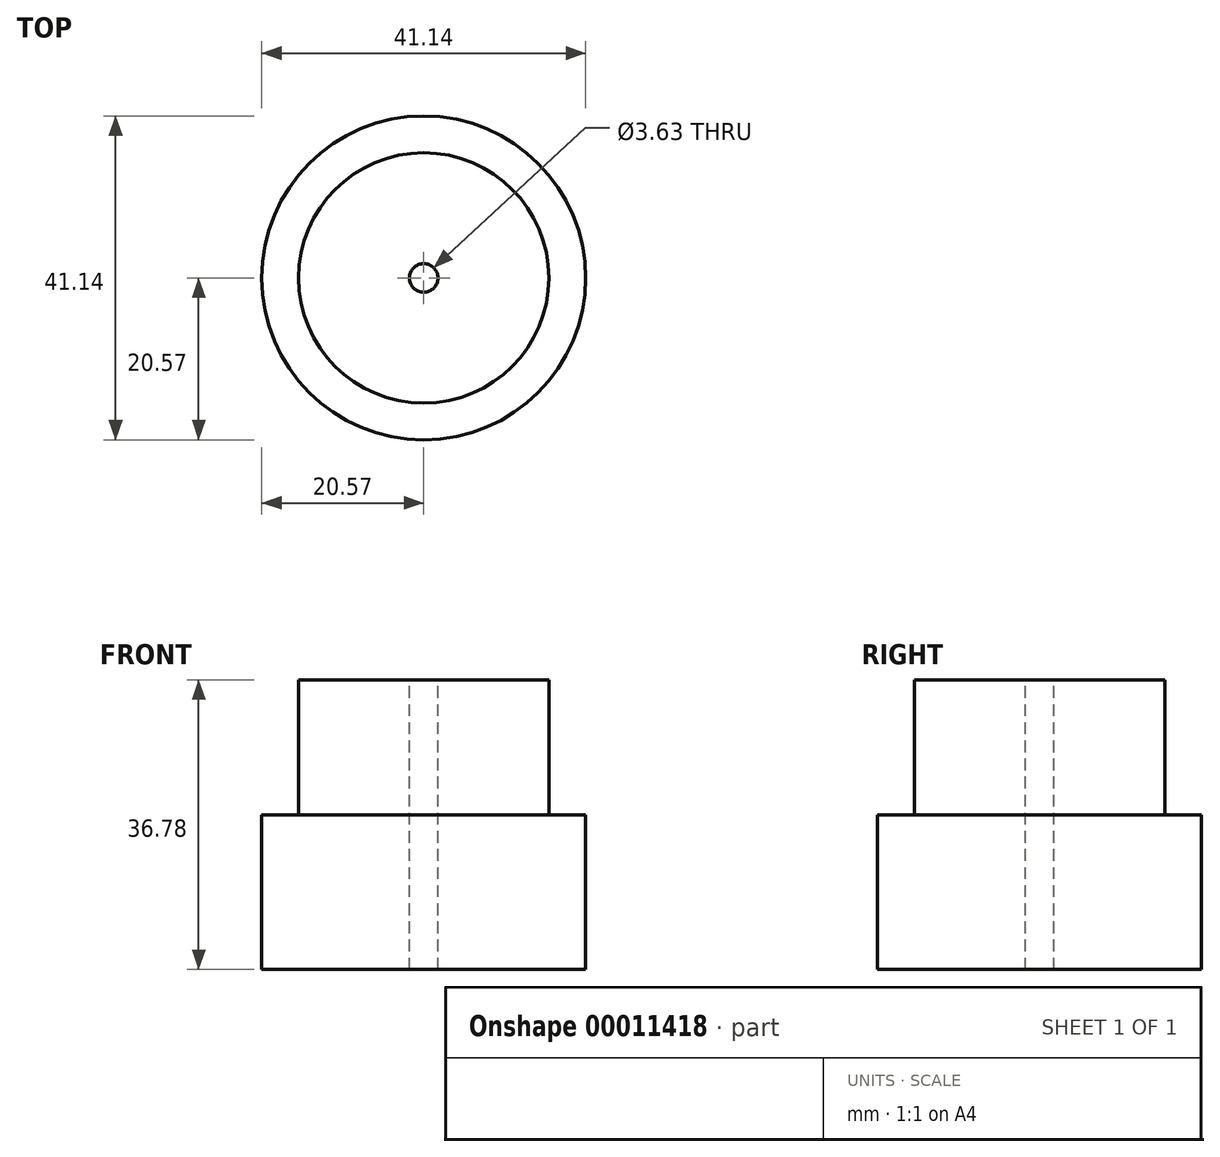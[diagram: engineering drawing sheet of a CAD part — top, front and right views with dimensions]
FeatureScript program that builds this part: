
annotation { "Feature Type Name" : "Feature", "Feature Type Description" : "" }
export const myFeature = defineFeature(function(context is Context, id is Id, definition is map)
    precondition{}
    {
        {
            var Q0;
            Q0=qCreatedBy(makeId("Top.planeOp"),FACE);
            var sketch = newSketch(context, id + "F0", { "sketchPlane" : qUnion([Q0])});
            skCircle(sketch, "E0", {"center": v(0, 0) * mm, "radius": 20.57 * mm});
            skSolve(sketch);
        }
        {
            var Q0;
            Q0 = qSketchRegion(id + "F0", true);
            extrude(context, id + "F1", {"entities" : qUnion([Q0]), "depth" : 19.66 * mm});
        }
        {
            var Q0;
            Q0=makeQuery(id+"F1.opExtrude","CAP_FACE",FACE,{"disambiguationData":[OSD([sQuery(id+"F0.wireOp",EDGE,"E0")])],"isStart":false});
            var sketch = newSketch(context, id + "F2", { "sketchPlane" : qUnion([Q0])});
            skCircle(sketch, "E1", {"center": v(0, 0) * mm, "radius": 15.9 * mm});
            skSolve(sketch);
        }
        {
            var Q0;
            Q0 = qSketchRegion(id + "F2", true);
            extrude(context, id + "F3", {"entities" : qUnion([Q0]), "operationType" : NewBodyOperationType.ADD, "depth" : 17.12 * mm});
        }
        {
            var Q0;
            Q0=makeQuery(id+"F3.opExtrude","CAP_FACE",FACE,{"disambiguationData":[OSD([sQuery(id+"F2.wireOp",EDGE,"E1")])],"isStart":false});
            var sketch = newSketch(context, id + "F4", { "sketchPlane" : qUnion([Q0])});
            skCircle(sketch, "E2", {"center": v(0, 0) * mm, "radius": 1.82 * mm});
            skSolve(sketch);
        }
        {
            var Q0;
            Q0 = qSketchRegion(id + "F4", true);
            extrude(context, id + "F5", {"entities" : qUnion([Q0]), "operationType" : NewBodyOperationType.REMOVE, "endBound" : BoundingType.UP_TO_NEXT, "oppositeDirection" : true, "depth" : 25.4 * mm});
        }
    });
